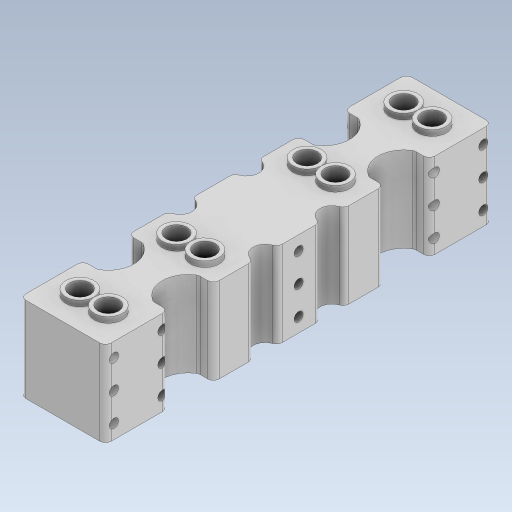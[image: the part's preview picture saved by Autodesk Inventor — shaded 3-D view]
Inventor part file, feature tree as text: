
AUTODESK INVENTOR PART (.ipt)
format: ipt  version: 2023.5 (Build 275446000, 446)  size: 685,056 bytes
history: native  units: mm
features: extrude x3, sketch x2, plane x1
ambient origin geometry x8: Origin, YZ Plane, XZ Plane, XY Plane, X Axis, Y Axis, Z Axis, Center Point
bodies: Solid1 (feature_tree)
feature tree (6):
  sketch  "Sketch1"  dims[d0=15.0mm d1=7.5mm]
  extrude  "Extrusion1"  Depth=7.5mm
  extrude  "Extrusion2"  Depth=10.0mm
  plane  "Work Plane1"
  extrude  "Extrusion3"  Depth=10.0mm
  sketch  "Sketch2"  dims[d2=7.3mm d3=23.0mm d4=10.0mm d6=7.3mm d7=10.0mm d8=34.0mm d9=4.0mm d10=4.0mm d11=2.0mm d12=2.0mm d13=30.0mm d14=0.0mm d15=32.0mm d16=0.0mm d17=3.2mm d18=3.2mm d19=5.0mm d20=3.2mm d21=3.2mm d22=3.2mm d23=3.2mm d24=32.0mm d25=0.0mm d26=3.2mm d27=3.2mm d28=3.2mm d29=3.2mm d30=3.2mm d31=3.2mm d32=3.2mm d33=3.2mm d34=3.2mm d35=2.0mm d36=2.0mm d37=2.0mm]
